# Revit family: LED QUADRATE 02_AM24W.2.32
name_source: partatom
category: Luminarias
units: mm (PartAtom-declared; Revit-internal decimal feet)

## family parameters
Compartido = No
Corte con vacíos al cargar = No
Cota de conector redondo = Diámetro de uso
Origen de luz = Sí
Punto de cálculo de habitación = No
Se basa en plano de trabajo = Sí
Siempre vertical = No
Tipo de pieza = Normal

## types (1)
- LED QUADRATE 02_AM24W.2.32
    Cambio de temperatura de color de luz atenuada = <Ninguno>
    Comentarios de vataje = 100-240V
    Descripción = LUMINARIA DIRIGIBLE TIPO ARBOTANTE, DOBLE HAZ DE LUZ (UP & DOWN), DE MATERIAL EN ALUMINIO FUNDIDO A PRESION CUBIERTO CON POLVO GRIS OSCURO Y VIDRIO DE 3MM, CON UN PESO DE 3KG, CON 2 LED TIPO NICHIA Y UNA POTENCIA TOTAL DE 26.5W, 2X1251 LUMENES, TEMPERATURA EN BLANCO CALIDO 3000K, IRC 80, IP 65, IK 06, APERTURA DE 32 GRADOS POR PROYECTO, CORRIENTE DE OPERACIÓN 211mA, CABLE DE 0.3M, ALIMENTADO A 100-240VAC
    Elevación por defecto = 0 mm  [stored 0 ft]
    Fabricante = BRILLANT
    Filtro de color = 16777215
    Longitud de símbolo de origen de luz = 1000 mm  [stored 3.28084 ft]
    Lámpara = NICHIA
    Modelo = AM24W.2.32
    Watt per fixture = 26.5
    Ángulo de campo de foco = 32.00°
    Ángulo de enfoque = 32.00°
    Ángulo de inclinación = 60.00°

note: [stored X ft] marks values corroborated as IEEE doubles in the binary element streams (Revit-internal decimal feet)

## geometry (parser evidence)
native form markers: Blend x2
no freeform markers — native parametric forms only
